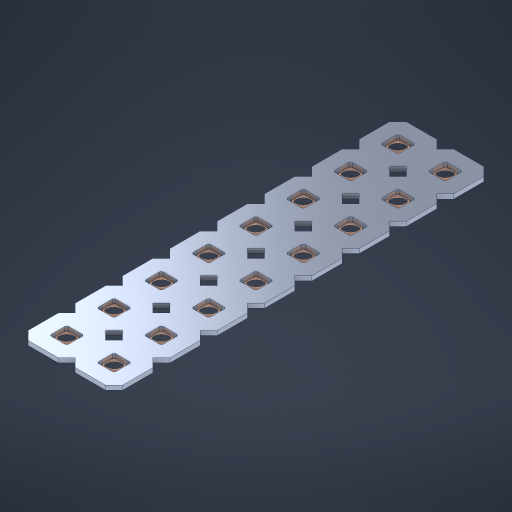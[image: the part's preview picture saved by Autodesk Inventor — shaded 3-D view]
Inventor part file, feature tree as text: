
AUTODESK INVENTOR PART (.ipt)
format: ipt  version: 2023 (Build 270158000, 158)  size: 434,176 bytes
history: native  units: in
note: dims shown in document units (in); Inventor stores cm internally (conversion verified against a paired STEP export)
features: other x17, extrude x15, sketch x2, pattern_linear x1
ambient origin geometry x8: Origin, YZ Plane, XZ Plane, XY Plane, X Axis, Y Axis, Z Axis, Center Point
bodies: Solid1 (feature_tree), Body (feature_tree)
feature tree (35):
  pattern_linear  "Rectangular Pattern1"  Spacing1=0.09in  [1 undecoded]
  sketch  "Sketch1"  dims[d1=0.5in]
  sketch  "Sketch2"  dims[d2=0.182in d3=0.09in d4=0.09in d5=0.09in d6=0.09in d7=0.09in d8=0.09in d9=0.09in d10=0.09in d11=0.02in d13=0.0in d14=0.172in d15=0.0625in d16=0.0in d19=0.5in d22=0.5in]
  other  "Srf1"
  other  "Srf126"
  other  "Srf127"
  other  "Srf128"
  other  "Srf129"
  other  "Srf130"
  other  "Srf131"
  other  "Srf250"
  other  "Srf268"
  other  "Srf269"
  other  "Srf270"
  other  "Srf271"
  other  "Srf272"
  other  "Srf273"
  other  "Srf274"
  other  "Srf275"
  other  "Circle"
  extrude  "ExtrusionSrf126"  Depth=0.09in
  extrude  "ExtrusionSrf127"  Depth=0.09in
  extrude  "ExtrusionSrf128"  Depth=0.09in
  extrude  "ExtrusionSrf129"  Depth=0.09in
  extrude  "ExtrusionSrf130"  Depth=0.09in
  extrude  "ExtrusionSrf131"  Depth=0.09in
  extrude  "ExtrusionSrf250"  Depth=0.09in
  extrude  "ExtrusionSrf268"  Depth=0.02in
  extrude  "ExtrusionSrf269"  TaperAngle=0.0deg  [1 undecoded]
  extrude  "ExtrusionSrf270"  Depth=0.5in
  extrude  "ExtrusionSrf271"  Depth=0.5in TaperAngle=0.0deg
  extrude  "ExtrusionSrf272"  Depth=0.5in
  extrude  "ExtrusionSrf273"  Depth=0.5in
  extrude  "ExtrusionSrf274"  [1 undecoded]
  extrude  "ExtrusionSrf275"  [1 undecoded]
note: 4 required parameter values undecoded (feature->parameter linkage not recoverable at this tier; creation-order binding heuristic only, values carry confidence <= 0.55)
